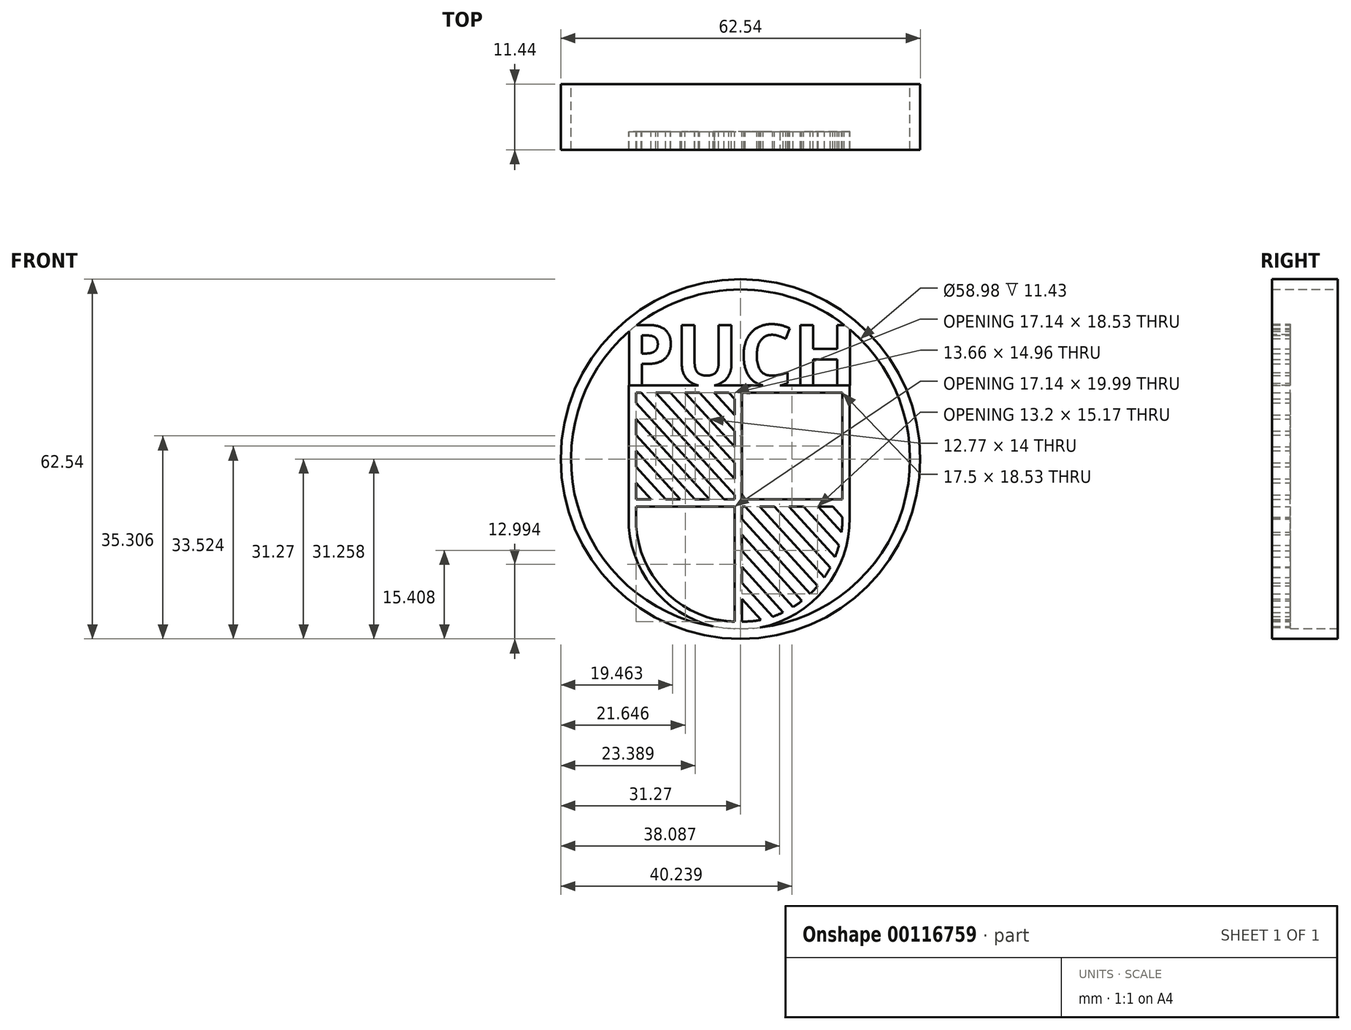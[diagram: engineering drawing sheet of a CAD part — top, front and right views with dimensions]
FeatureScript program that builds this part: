
annotation { "Feature Type Name" : "Feature", "Feature Type Description" : "" }
export const myFeature = defineFeature(function(context is Context, id is Id, definition is map)
    precondition{}
    {
        {
            var Q0;
            Q0=qCreatedBy(makeId("Front.planeOp"),FACE);
            var sketch = newSketch(context, id + "F0", { "sketchPlane" : qUnion([Q0])});
            skArc(sketch, "E0", {"start": v(3.43, -29.29) * mm, "mid": v(0.67, 29.48) * mm, "end": v(-4.76, -29.1) * mm});
            skText(sketch, "E1", { "text": "PUCH", "fontName": "OpenSans-Bold.ttf"});
            skLineSegment(sketch, "E2", {"start": v(-19.46, 12.79) * mm, "end": v(19, 12.79) * mm});
            skLineSegment(sketch, "E3", {"start": v(19, 12.79) * mm, "end": v(19, -10.14) * mm});
            skLineSegment(sketch, "E4", {"start": v(-19.46, -10.14) * mm, "end": v(-19.46, 12.79) * mm});
            skArc(sketch, "E5", {"start": v(-19.46, -10.14) * mm, "mid": v(-15.43, -22.2) * mm, "end": v(-4.76, -29.1) * mm});
            skPoint(sketch, "E6.orphan", {"position": v(-19.46, -14.32) * mm});
            skArc(sketch, "E7.trimOffspring", {"start": v(3.43, -29.29) * mm, "mid": v(14.69, -22.54) * mm, "end": v(19, -10.14) * mm});
            skArc(sketch, "E8.0", {"start": v(-18.2, -10.16) * mm, "mid": v(-14.43, -21.42) * mm, "end": v(-4.46, -27.87) * mm});
            skArc(sketch, "E9.0", {"start": v(3.19, -28.04) * mm, "mid": v(3.37, -28) * mm, "end": v(3.55, -27.97) * mm});
            skLineSegment(sketch, "E10.0", {"start": v(17.72, 11.52) * mm, "end": v(17.72, -7) * mm});
            skLineSegment(sketch, "E11.0", {"start": v(-18.2, 11.52) * mm, "end": v(-17.25, 11.52) * mm});
            skCircle(sketch, "E12.0", {"center": v(0, 0) * mm, "radius": 31.27 * mm});
            skArc(sketch, "E13", {"start": v(-4.46, -27.87) * mm, "mid": v(-2.77, -28.14) * mm, "end": v(-1.05, -28.27) * mm});
            skLineSegment(sketch, "E14.0", {"start": v(-18.2, -8.28) * mm, "end": v(-1.05, -8.28) * mm});
            skLineSegment(sketch, "E15.0", {"start": v(-1.05, 10.47) * mm, "end": v(-1.05, 7.68) * mm});
            skLineSegment(sketch, "E16.0", {"start": v(0.22, 11.52) * mm, "end": v(0.22, -7) * mm});
            skLineSegment(sketch, "E17.0", {"start": v(-18.2, -7) * mm, "end": v(-15.58, -7) * mm});
            skLineSegment(sketch, "E18.trimOffspring", {"start": v(-18.2, -7) * mm, "end": v(-18.2, -4.15) * mm});
            skLineSegment(sketch, "E19.trimOffspring", {"start": v(-1.05, -8.28) * mm, "end": v(-1.05, -28.29) * mm});
            skLineSegment(sketch, "E20.trimOffspring", {"start": v(0.22, -7) * mm, "end": v(17.72, -7) * mm});
            skLineSegment(sketch, "E21.trimOffspring", {"start": v(0.22, -8.28) * mm, "end": v(0.22, -10.4) * mm});
            skLineSegment(sketch, "E22.trimOffspring", {"start": v(0.22, -8.28) * mm, "end": v(0.82, -8.28) * mm});
            skLineSegment(sketch, "E23.trimOffspring", {"start": v(0.22, 11.52) * mm, "end": v(17.72, 11.52) * mm});
            skArc(sketch, "E24.trimOffspring", {"start": v(0.22, -28.29) * mm, "mid": v(1.7, -28.21) * mm, "end": v(3.19, -28.04) * mm});
            skLineSegment(sketch, "E25", {"start": v(-18.2, -4.15) * mm, "end": v(-15.58, -7) * mm});
            skLineSegment(sketch, "E26.1.0.0", {"start": v(-18.2, -1.36) * mm, "end": v(-13.04, -7) * mm});
            skLineSegment(sketch, "E26.2.0.0", {"start": v(-18.2, 1.42) * mm, "end": v(-10.5, -7) * mm});
            skLineSegment(sketch, "E26.3.0.0", {"start": v(-18.2, 4.2) * mm, "end": v(-7.96, -7) * mm});
            skLineSegment(sketch, "E26.4.0.0", {"start": v(-18.2, 6.99) * mm, "end": v(-5.42, -7) * mm});
            skLineSegment(sketch, "E26.5.0.0", {"start": v(-18.2, 9.77) * mm, "end": v(-2.88, -7) * mm});
            skLineSegment(sketch, "E26.6.0.0", {"start": v(-17.25, 11.52) * mm, "end": v(-0.34, -7) * mm});
            skLineSegment(sketch, "E26.7.0.0", {"start": v(-14.71, 11.52) * mm, "end": v(-1.05, -3.45) * mm});
            skLineSegment(sketch, "E26.8.0.0", {"start": v(-12.17, 11.52) * mm, "end": v(-1.05, -0.66) * mm});
            skLineSegment(sketch, "E26.9.0.0", {"start": v(-9.63, 11.52) * mm, "end": v(-1.05, 2.12) * mm});
            skLineSegment(sketch, "E26.10.0.0", {"start": v(-7.1, 11.52) * mm, "end": v(-1.05, 4.9) * mm});
            skLineSegment(sketch, "E26.11.0.0", {"start": v(-4.55, 11.52) * mm, "end": v(-1.05, 7.68) * mm});
            skLineSegment(sketch, "E26.12.0.0", {"start": v(-2.01, 11.52) * mm, "end": v(-1.05, 10.47) * mm});
            skPoint(sketch, "E27.orphan", {"position": v(-15.65, -4.15) * mm});
            skPoint(sketch, "E28.orphan", {"position": v(-13.11, -4.15) * mm});
            skPoint(sketch, "E29.orphan", {"position": v(-10.57, -4.15) * mm});
            skPoint(sketch, "E30.orphan", {"position": v(-8.03, -4.15) * mm});
            skPoint(sketch, "E31.orphan", {"position": v(-5.5, -4.15) * mm});
            skPoint(sketch, "E32.orphan", {"position": v(-2.95, -4.15) * mm});
            skPoint(sketch, "E33.orphan", {"position": v(-0.41, -4.15) * mm});
            skPoint(sketch, "E34.orphan", {"position": v(2.13, -4.15) * mm});
            skPoint(sketch, "E35.orphan", {"position": v(4.67, -4.15) * mm});
            skPoint(sketch, "E36.orphan", {"position": v(7.2, -4.15) * mm});
            skPoint(sketch, "E37.orphan", {"position": v(9.75, -4.15) * mm});
            skPoint(sketch, "E38.orphan", {"position": v(12.29, -4.15) * mm});
            skPoint(sketch, "E39.orphan", {"position": v(-10.5, -7) * mm});
            skPoint(sketch, "E40.orphan", {"position": v(-7.96, -7) * mm});
            skPoint(sketch, "E41.orphan", {"position": v(-5.42, -7) * mm});
            skPoint(sketch, "E42.orphan", {"position": v(-2.88, -7) * mm});
            skPoint(sketch, "E43.orphan", {"position": v(-0.34, -7) * mm});
            skPoint(sketch, "E44.orphan", {"position": v(2.2, -7) * mm});
            skPoint(sketch, "E45.orphan", {"position": v(4.74, -7) * mm});
            skPoint(sketch, "E46.orphan", {"position": v(7.28, -7) * mm});
            skPoint(sketch, "E47.orphan", {"position": v(9.82, -7) * mm});
            skPoint(sketch, "E48.orphan", {"position": v(12.36, -7) * mm});
            skPoint(sketch, "E49.orphan", {"position": v(14.9, -7) * mm});
            skLineSegment(sketch, "E50.trimOffspring", {"start": v(3.36, -8.28) * mm, "end": v(14.58, -20.57) * mm});
            skLineSegment(sketch, "E51.trimOffspring", {"start": v(5.9, -8.28) * mm, "end": v(15.6, -18.9) * mm});
            skLineSegment(sketch, "E52.trimOffspring", {"start": v(8.44, -8.28) * mm, "end": v(16.45, -17.06) * mm});
            skLineSegment(sketch, "E53.trimOffspring", {"start": v(10.98, -8.28) * mm, "end": v(17.12, -15.01) * mm});
            skLineSegment(sketch, "E54.trimOffspring", {"start": v(13.52, -8.28) * mm, "end": v(17.57, -12.72) * mm});
            skLineSegment(sketch, "E55.trimOffspring", {"start": v(16.06, -8.28) * mm, "end": v(17.72, -10.1) * mm});
            skLineSegment(sketch, "E56.trimOffspring", {"start": v(0.22, -24.32) * mm, "end": v(3.55, -27.97) * mm});
            skLineSegment(sketch, "E57.trimOffspring", {"start": v(0.22, -21.54) * mm, "end": v(5.58, -27.4) * mm});
            skLineSegment(sketch, "E58.trimOffspring", {"start": v(0.22, -18.75) * mm, "end": v(7.43, -26.65) * mm});
            skLineSegment(sketch, "E59.trimOffspring", {"start": v(0.22, -15.97) * mm, "end": v(9.13, -25.74) * mm});
            skLineSegment(sketch, "E60.trimOffspring", {"start": v(0.22, -13.19) * mm, "end": v(10.7, -24.66) * mm});
            skLineSegment(sketch, "E61.trimOffspring", {"start": v(0.22, -10.4) * mm, "end": v(12.12, -23.44) * mm});
            skLineSegment(sketch, "E62.trimOffspring", {"start": v(0.82, -8.28) * mm, "end": v(13.42, -22.08) * mm});
            skLineSegment(sketch, "E63.trimOffspring", {"start": v(-18.2, -1.36) * mm, "end": v(-18.2, 1.42) * mm});
            skLineSegment(sketch, "E64.trimOffspring", {"start": v(-7.96, -7) * mm, "end": v(-5.42, -7) * mm});
            skLineSegment(sketch, "E65.trimOffspring", {"start": v(-18.2, 4.2) * mm, "end": v(-18.2, 6.99) * mm});
            skLineSegment(sketch, "E66.trimOffspring", {"start": v(-18.2, 9.77) * mm, "end": v(-18.2, 11.52) * mm});
            skLineSegment(sketch, "E67.trimOffspring", {"start": v(-2.88, -7) * mm, "end": v(-1.05, -7) * mm});
            skLineSegment(sketch, "E68.trimOffspring", {"start": v(-1.05, -6.23) * mm, "end": v(-1.05, -7) * mm});
            skLineSegment(sketch, "E69.trimOffspring", {"start": v(-14.71, 11.52) * mm, "end": v(-12.17, 11.52) * mm});
            skLineSegment(sketch, "E70.trimOffspring", {"start": v(-9.63, 11.52) * mm, "end": v(-7.1, 11.52) * mm});
            skLineSegment(sketch, "E71.trimOffspring", {"start": v(-1.05, -0.66) * mm, "end": v(-1.05, -3.45) * mm});
            skLineSegment(sketch, "E72.trimOffspring", {"start": v(-1.05, 4.9) * mm, "end": v(-1.05, 2.12) * mm});
            skLineSegment(sketch, "E73.trimOffspring", {"start": v(-4.55, 11.52) * mm, "end": v(-2.01, 11.52) * mm});
            skLineSegment(sketch, "E74.trimOffspring", {"start": v(-13.04, -7) * mm, "end": v(-10.5, -7) * mm});
            skLineSegment(sketch, "E75.trimOffspring", {"start": v(0.22, -24.32) * mm, "end": v(0.22, -28.29) * mm});
            skArc(sketch, "E76.trimOffspring", {"start": v(5.58, -27.4) * mm, "mid": v(6.51, -27.06) * mm, "end": v(7.43, -26.65) * mm});
            skArc(sketch, "E77.trimOffspring", {"start": v(9.13, -25.74) * mm, "mid": v(9.93, -25.22) * mm, "end": v(10.7, -24.66) * mm});
            skLineSegment(sketch, "E78.trimOffspring", {"start": v(0.22, -18.75) * mm, "end": v(0.22, -21.54) * mm});
            skArc(sketch, "E79.trimOffspring", {"start": v(12.12, -23.44) * mm, "mid": v(12.79, -22.78) * mm, "end": v(13.42, -22.08) * mm});
            skArc(sketch, "E80.trimOffspring", {"start": v(14.58, -20.57) * mm, "mid": v(15.1, -19.75) * mm, "end": v(15.6, -18.9) * mm});
            skLineSegment(sketch, "E81.trimOffspring", {"start": v(3.36, -8.28) * mm, "end": v(5.9, -8.28) * mm});
            skLineSegment(sketch, "E82.trimOffspring", {"start": v(8.44, -8.28) * mm, "end": v(10.98, -8.28) * mm});
            skArc(sketch, "E83.trimOffspring", {"start": v(16.45, -17.06) * mm, "mid": v(16.82, -16.04) * mm, "end": v(17.12, -15.01) * mm});
            skArc(sketch, "E84.trimOffspring", {"start": v(17.57, -12.72) * mm, "mid": v(17.7, -11.44) * mm, "end": v(17.72, -10.16) * mm});
            skLineSegment(sketch, "E85.trimOffspring", {"start": v(13.52, -8.28) * mm, "end": v(16.06, -8.28) * mm});
            skLineSegment(sketch, "E86", {"start": v(-18.2, -10.16) * mm, "end": v(-18.2, -8.28) * mm});
            skLineSegment(sketch, "E87", {"start": v(0.22, -13.19) * mm, "end": v(0.22, -15.97) * mm});
            skLineSegment(sketch, "E88", {"start": v(17.72, -10.16) * mm, "end": v(17.72, -10.1) * mm});
            const initialGuessF0  = {"E1": [-0.02073, 0.01279, 1, 0, 0.01062]};
            skSetInitialGuess(sketch, initialGuessF0);
            skSolve(sketch);
        }
        {
            var Q0;
            Q0=makeQuery(id+"F0.imprint","IMPRINT",FACE,{"disambiguationData":[TD([[makeQuery(id+"F0.imprint","IMPRINT",EDGE,{"derivedFrom":sQuery(id+"F0.wireOp",EDGE,"E1.sketch_text.stroke-0")}),-1.0]])]});
            var Q1;
            Q1=makeQuery(id+"F0.imprint","IMPRINT",FACE,{"disambiguationData":[TD([[makeQuery(id+"F0.imprint","IMPRINT",EDGE,{"derivedFrom":sQuery(id+"F0.wireOp",EDGE,"E1.sketch_text.stroke-16")}),-1.0]])]});
            var Q2;
            Q2=makeQuery(id+"F0.imprint","IMPRINT",FACE,{"disambiguationData":[TD([[makeQuery(id+"F0.imprint","IMPRINT",EDGE,{"derivedFrom":sQuery(id+"F0.wireOp",EDGE,"E1.sketch_text.stroke-31")}),-1.0]])]});
            var Q3;
            {var subQ2=sQuery(id+"F0.wireOp",EDGE,"E1.sketch_text.stroke-46");Q3=makeQuery(id+"F0.imprint","IMPRINT",FACE,{"disambiguationData":[TD([[makeQuery(id+"F0.imprint","IMPRINT",EDGE,{"derivedFrom":subQ2}),-1.0]])]});}
            var Q4;
            {var subQ0=sQuery(id+"F0.wireOp",EDGE,"E1.sketch_text.stroke-57");var subQ1=sQuery(id+"F0.wireOp",EDGE,"E0");var subQ2=makeQuery(id+"F0.imprint","INTERSECT",VERTEX,{"derivedFrom":[subQ1,subQ0]});Q4=makeQuery(id+"F0.imprint","IMPRINT",FACE,{"disambiguationData":[TD([[makeQuery(id+"F0.imprint","IMPRINT",EDGE,{"disambiguationData":[TD([[subQ2,-1.0]])],"derivedFrom":subQ1}),-1.0]])]});}
            var Q5;
            {var subQ0=sQuery(id+"F0.wireOp",EDGE,"E1.sketch_text.stroke-37");var subQ1=sQuery(id+"F0.wireOp",EDGE,"E1.sketch_text.stroke-36");var subQ2=makeQuery(id+"F0.imprint","INTERSECT",VERTEX,{"derivedFrom":[subQ1,subQ0]});Q5=makeQuery(id+"F0.imprint","IMPRINT",FACE,{"disambiguationData":[TD([[makeQuery(id+"F0.imprint","IMPRINT",EDGE,{"disambiguationData":[TD([[subQ2,1.0]])],"derivedFrom":subQ1}),-1.0]])]});}
            var Q6;
            {var subQ0=sQuery(id+"F0.wireOp",EDGE,"E1.sketch_text.stroke-20");var subQ1=sQuery(id+"F0.wireOp",EDGE,"E1.sketch_text.stroke-19");var subQ2=makeQuery(id+"F0.imprint","INTERSECT",VERTEX,{"derivedFrom":[subQ1,subQ0]});Q6=makeQuery(id+"F0.imprint","IMPRINT",FACE,{"disambiguationData":[TD([[makeQuery(id+"F0.imprint","IMPRINT",EDGE,{"disambiguationData":[TD([[subQ2,1.0]])],"derivedFrom":subQ1}),-1.0]])]});}
            var Q7;
            {var subQ0=sQuery(id+"F0.wireOp",EDGE,"E1.sketch_text.stroke-13");var subQ1=sQuery(id+"F0.wireOp",EDGE,"E0");var subQ2=makeQuery(id+"F0.imprint","INTERSECT",VERTEX,{"derivedFrom":[subQ1,subQ0]});Q7=makeQuery(id+"F0.imprint","IMPRINT",FACE,{"disambiguationData":[TD([[makeQuery(id+"F0.imprint","IMPRINT",EDGE,{"disambiguationData":[TD([[subQ2,-1.0]])],"derivedFrom":subQ1}),-1.0]])]});}
            var Q8;
            {var subQ27=sQuery(id+"F0.wireOp",EDGE,"E3");Q8=makeQuery(id+"F0.imprint","IMPRINT",FACE,{"disambiguationData":[TD([[makeQuery(id+"F0.imprint","IMPRINT",EDGE,{"derivedFrom":subQ27}),-1.0]])]});}
            extrude(context, id + "F1", {"entities" : qUnion([Q0, Q1, Q2, Q3, Q4, Q5, Q6, Q7, Q8]), "depth" : 3.17 * mm});
        }
        {
            var Q0;
            Q0=makeQuery(id+"F1.opExtrude","CAP_FACE",FACE,{"disambiguationData":[OSD([sQuery(id+"F0.wireOp",EDGE,"E0"),sQuery(id+"F0.wireOp",EDGE,"E1.sketch_text.stroke-0"),sQuery(id+"F0.wireOp",EDGE,"E1.sketch_text.stroke-1"),sQuery(id+"F0.wireOp",EDGE,"E1.sketch_text.stroke-2"),sQuery(id+"F0.wireOp",EDGE,"E1.sketch_text.stroke-3"),sQuery(id+"F0.wireOp",EDGE,"E1.sketch_text.stroke-4"),sQuery(id+"F0.wireOp",EDGE,"E1.sketch_text.stroke-5"),sQuery(id+"F0.wireOp",EDGE,"E1.sketch_text.stroke-6"),sQuery(id+"F0.wireOp",EDGE,"E1.sketch_text.stroke-7"),sQuery(id+"F0.wireOp",EDGE,"E1.sketch_text.stroke-8"),sQuery(id+"F0.wireOp",EDGE,"E1.sketch_text.stroke-9"),sQuery(id+"F0.wireOp",EDGE,"E1.sketch_text.stroke-10"),sQuery(id+"F0.wireOp",EDGE,"E1.sketch_text.stroke-12"),sQuery(id+"F0.wireOp",EDGE,"E1.sketch_text.stroke-13"),sQuery(id+"F0.wireOp",EDGE,"E1.sketch_text.stroke-14"),sQuery(id+"F0.wireOp",EDGE,"E1.sketch_text.stroke-15"),sQuery(id+"F0.wireOp",EDGE,"E1.sketch_text.stroke-16"),sQuery(id+"F0.wireOp",EDGE,"E1.sketch_text.stroke-17"),sQuery(id+"F0.wireOp",EDGE,"E1.sketch_text.stroke-18"),sQuery(id+"F0.wireOp",EDGE,"E1.sketch_text.stroke-19"),sQuery(id+"F0.wireOp",EDGE,"E1.sketch_text.stroke-20"),sQuery(id+"F0.wireOp",EDGE,"E1.sketch_text.stroke-21"),sQuery(id+"F0.wireOp",EDGE,"E1.sketch_text.stroke-22"),sQuery(id+"F0.wireOp",EDGE,"E1.sketch_text.stroke-23"),sQuery(id+"F0.wireOp",EDGE,"E1.sketch_text.stroke-24"),sQuery(id+"F0.wireOp",EDGE,"E1.sketch_text.stroke-25"),sQuery(id+"F0.wireOp",EDGE,"E1.sketch_text.stroke-26"),sQuery(id+"F0.wireOp",EDGE,"E1.sketch_text.stroke-27"),sQuery(id+"F0.wireOp",EDGE,"E1.sketch_text.stroke-28"),sQuery(id+"F0.wireOp",EDGE,"E1.sketch_text.stroke-29"),sQuery(id+"F0.wireOp",EDGE,"E1.sketch_text.stroke-30"),sQuery(id+"F0.wireOp",EDGE,"E1.sketch_text.stroke-31"),sQuery(id+"F0.wireOp",EDGE,"E1.sketch_text.stroke-32"),sQuery(id+"F0.wireOp",EDGE,"E1.sketch_text.stroke-33"),sQuery(id+"F0.wireOp",EDGE,"E1.sketch_text.stroke-34"),sQuery(id+"F0.wireOp",EDGE,"E1.sketch_text.stroke-35"),sQuery(id+"F0.wireOp",EDGE,"E1.sketch_text.stroke-36"),sQuery(id+"F0.wireOp",EDGE,"E1.sketch_text.stroke-37"),sQuery(id+"F0.wireOp",EDGE,"E1.sketch_text.stroke-38"),sQuery(id+"F0.wireOp",EDGE,"E1.sketch_text.stroke-39"),sQuery(id+"F0.wireOp",EDGE,"E1.sketch_text.stroke-40"),sQuery(id+"F0.wireOp",EDGE,"E1.sketch_text.stroke-41"),sQuery(id+"F0.wireOp",EDGE,"E1.sketch_text.stroke-42"),sQuery(id+"F0.wireOp",EDGE,"E1.sketch_text.stroke-43"),sQuery(id+"F0.wireOp",EDGE,"E1.sketch_text.stroke-44"),sQuery(id+"F0.wireOp",EDGE,"E1.sketch_text.stroke-45"),sQuery(id+"F0.wireOp",EDGE,"E1.sketch_text.stroke-46"),sQuery(id+"F0.wireOp",EDGE,"E1.sketch_text.stroke-47"),sQuery(id+"F0.wireOp",EDGE,"E1.sketch_text.stroke-48"),sQuery(id+"F0.wireOp",EDGE,"E1.sketch_text.stroke-49"),sQuery(id+"F0.wireOp",EDGE,"E1.sketch_text.stroke-51"),sQuery(id+"F0.wireOp",EDGE,"E1.sketch_text.stroke-52"),sQuery(id+"F0.wireOp",EDGE,"E1.sketch_text.stroke-53"),sQuery(id+"F0.wireOp",EDGE,"E1.sketch_text.stroke-54"),sQuery(id+"F0.wireOp",EDGE,"E1.sketch_text.stroke-55"),sQuery(id+"F0.wireOp",EDGE,"E1.sketch_text.stroke-56"),sQuery(id+"F0.wireOp",EDGE,"E1.sketch_text.stroke-57"),sQuery(id+"F0.wireOp",EDGE,"E2"),sQuery(id+"F0.wireOp",EDGE,"E3"),sQuery(id+"F0.wireOp",EDGE,"E4"),sQuery(id+"F0.wireOp",EDGE,"E5"),sQuery(id+"F0.wireOp",EDGE,"E7.trimOffspring"),sQuery(id+"F0.wireOp",EDGE,"E8.0"),sQuery(id+"F0.wireOp",EDGE,"E9.0"),sQuery(id+"F0.wireOp",EDGE,"E10.0"),sQuery(id+"F0.wireOp",EDGE,"E11.0"),sQuery(id+"F0.wireOp",EDGE,"E12.0"),sQuery(id+"F0.wireOp",EDGE,"E13"),sQuery(id+"F0.wireOp",EDGE,"E14.0"),sQuery(id+"F0.wireOp",EDGE,"E15.0"),sQuery(id+"F0.wireOp",EDGE,"E16.0"),sQuery(id+"F0.wireOp",EDGE,"E17.0"),sQuery(id+"F0.wireOp",EDGE,"E18.trimOffspring"),sQuery(id+"F0.wireOp",EDGE,"E19.trimOffspring"),sQuery(id+"F0.wireOp",EDGE,"E20.trimOffspring"),sQuery(id+"F0.wireOp",EDGE,"E21.trimOffspring"),sQuery(id+"F0.wireOp",EDGE,"E22.trimOffspring"),sQuery(id+"F0.wireOp",EDGE,"E23.trimOffspring"),sQuery(id+"F0.wireOp",EDGE,"E24.trimOffspring"),sQuery(id+"F0.wireOp",EDGE,"E25"),sQuery(id+"F0.wireOp",EDGE,"E26.1.0.0"),sQuery(id+"F0.wireOp",EDGE,"E26.2.0.0"),sQuery(id+"F0.wireOp",EDGE,"E26.3.0.0"),sQuery(id+"F0.wireOp",EDGE,"E26.4.0.0"),sQuery(id+"F0.wireOp",EDGE,"E26.5.0.0"),sQuery(id+"F0.wireOp",EDGE,"E26.6.0.0"),sQuery(id+"F0.wireOp",EDGE,"E26.7.0.0"),sQuery(id+"F0.wireOp",EDGE,"E26.8.0.0"),sQuery(id+"F0.wireOp",EDGE,"E26.9.0.0"),sQuery(id+"F0.wireOp",EDGE,"E26.10.0.0"),sQuery(id+"F0.wireOp",EDGE,"E26.11.0.0"),sQuery(id+"F0.wireOp",EDGE,"E26.12.0.0"),sQuery(id+"F0.wireOp",EDGE,"E50.trimOffspring"),sQuery(id+"F0.wireOp",EDGE,"E51.trimOffspring"),sQuery(id+"F0.wireOp",EDGE,"E52.trimOffspring"),sQuery(id+"F0.wireOp",EDGE,"E53.trimOffspring"),sQuery(id+"F0.wireOp",EDGE,"E54.trimOffspring"),sQuery(id+"F0.wireOp",EDGE,"E55.trimOffspring"),sQuery(id+"F0.wireOp",EDGE,"E56.trimOffspring"),sQuery(id+"F0.wireOp",EDGE,"E57.trimOffspring"),sQuery(id+"F0.wireOp",EDGE,"E58.trimOffspring"),sQuery(id+"F0.wireOp",EDGE,"E59.trimOffspring"),sQuery(id+"F0.wireOp",EDGE,"E60.trimOffspring"),sQuery(id+"F0.wireOp",EDGE,"E61.trimOffspring"),sQuery(id+"F0.wireOp",EDGE,"E62.trimOffspring"),sQuery(id+"F0.wireOp",EDGE,"E63.trimOffspring"),sQuery(id+"F0.wireOp",EDGE,"E64.trimOffspring"),sQuery(id+"F0.wireOp",EDGE,"E65.trimOffspring"),sQuery(id+"F0.wireOp",EDGE,"E66.trimOffspring"),sQuery(id+"F0.wireOp",EDGE,"E67.trimOffspring"),sQuery(id+"F0.wireOp",EDGE,"E68.trimOffspring"),sQuery(id+"F0.wireOp",EDGE,"E69.trimOffspring"),sQuery(id+"F0.wireOp",EDGE,"E70.trimOffspring"),sQuery(id+"F0.wireOp",EDGE,"E71.trimOffspring"),sQuery(id+"F0.wireOp",EDGE,"E72.trimOffspring"),sQuery(id+"F0.wireOp",EDGE,"E73.trimOffspring"),sQuery(id+"F0.wireOp",EDGE,"E74.trimOffspring"),sQuery(id+"F0.wireOp",EDGE,"E75.trimOffspring"),sQuery(id+"F0.wireOp",EDGE,"E76.trimOffspring"),sQuery(id+"F0.wireOp",EDGE,"E77.trimOffspring"),sQuery(id+"F0.wireOp",EDGE,"E78.trimOffspring"),sQuery(id+"F0.wireOp",EDGE,"E79.trimOffspring"),sQuery(id+"F0.wireOp",EDGE,"E80.trimOffspring"),sQuery(id+"F0.wireOp",EDGE,"E81.trimOffspring"),sQuery(id+"F0.wireOp",EDGE,"E82.trimOffspring"),sQuery(id+"F0.wireOp",EDGE,"E83.trimOffspring"),sQuery(id+"F0.wireOp",EDGE,"E84.trimOffspring"),sQuery(id+"F0.wireOp",EDGE,"E85.trimOffspring"),sQuery(id+"F0.wireOp",EDGE,"E86"),sQuery(id+"F0.wireOp",EDGE,"E87"),sQuery(id+"F0.wireOp",EDGE,"E88")])],"isStart":true});
            var sketch = newSketch(context, id + "F2", { "sketchPlane" : qUnion([Q0])});
            skCircle(sketch, "E89", {"center": v(0, 0) * mm, "radius": 29.49 * mm});
            skCircle(sketch, "E90", {"center": v(0, 0) * mm, "radius": 31.27 * mm});
            skSolve(sketch);
        }
        {
            var Q0;
            Q0 = qSketchRegion(id + "F2", true);
            extrude(context, id + "F3", {"entities" : qUnion([Q0]), "operationType" : NewBodyOperationType.ADD, "depth" : 8.25 * mm});
        }
    });
